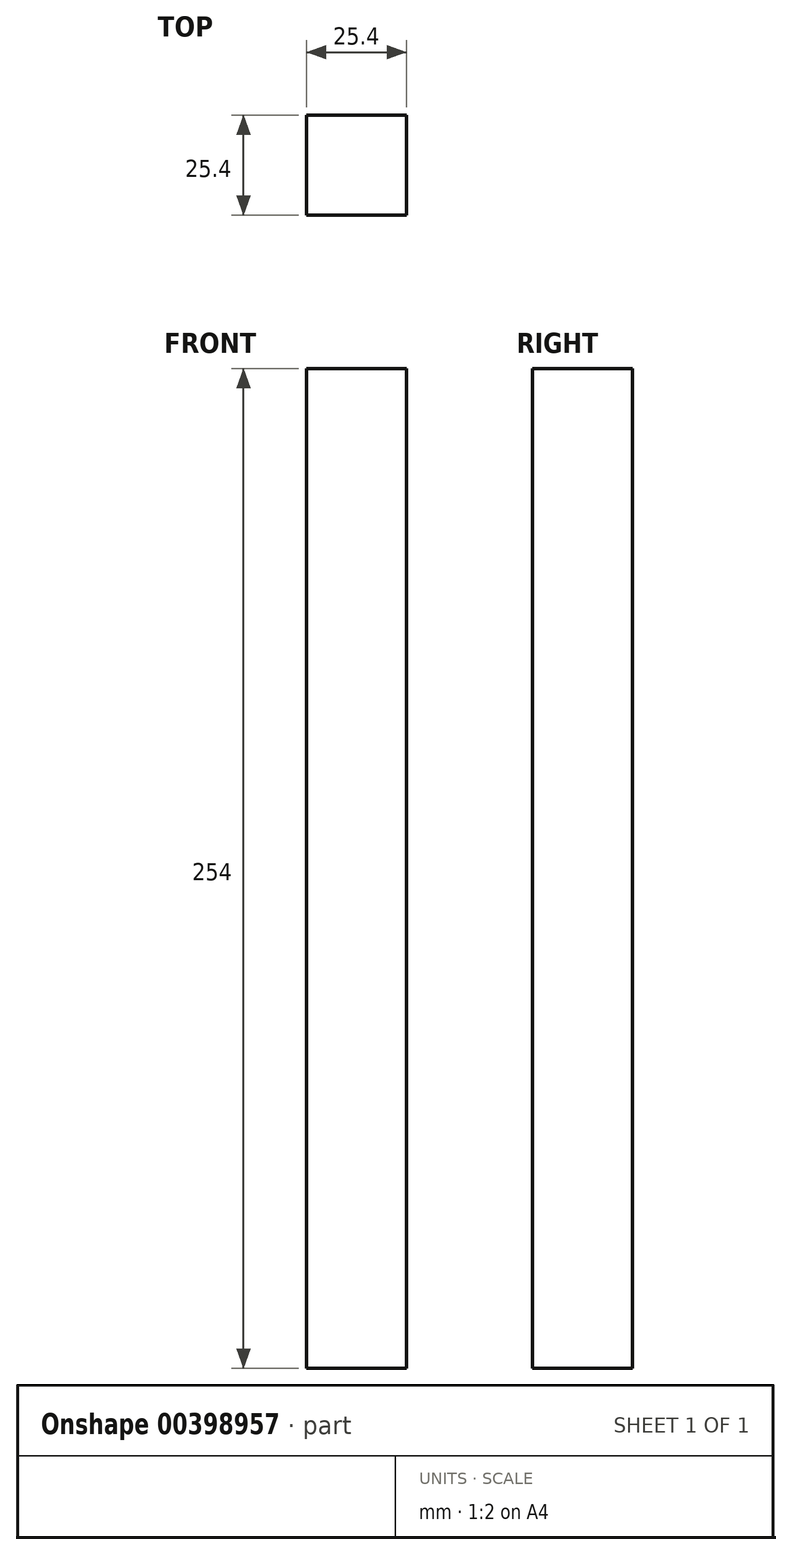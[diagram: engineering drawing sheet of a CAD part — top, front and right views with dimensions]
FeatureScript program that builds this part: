
annotation { "Feature Type Name" : "Feature", "Feature Type Description" : "" }
export const myFeature = defineFeature(function(context is Context, id is Id, definition is map)
    precondition{}
    {
        {
            var Q0;
            Q0=qCreatedBy(makeId("Front.planeOp"),FACE);
            var sketch = newSketch(context, id + "F0", { "sketchPlane" : qUnion([Q0])});
            skLineSegment(sketch, "E0.bottom", {"start": v(12.7, 127) * mm, "end": v(-12.7, 127) * mm});
            skLineSegment(sketch, "E0.top", {"start": v(12.7, -127) * mm, "end": v(-12.7, -127) * mm});
            skLineSegment(sketch, "E0.left", {"start": v(12.7, 127) * mm, "end": v(12.7, -127) * mm});
            skLineSegment(sketch, "E0.right", {"start": v(-12.7, 127) * mm, "end": v(-12.7, -127) * mm});
            skPoint(sketch, "E0.middle", {"position": v(0, 0) * mm});
            skSolve(sketch);
        }
        {
            var Q0;
            Q0 = qSketchRegion(id + "F0", true);
            extrude(context, id + "F1", {"entities" : qUnion([Q0]), "depth" : 25.4 * mm, "symmetric" : true});
        }
    });
